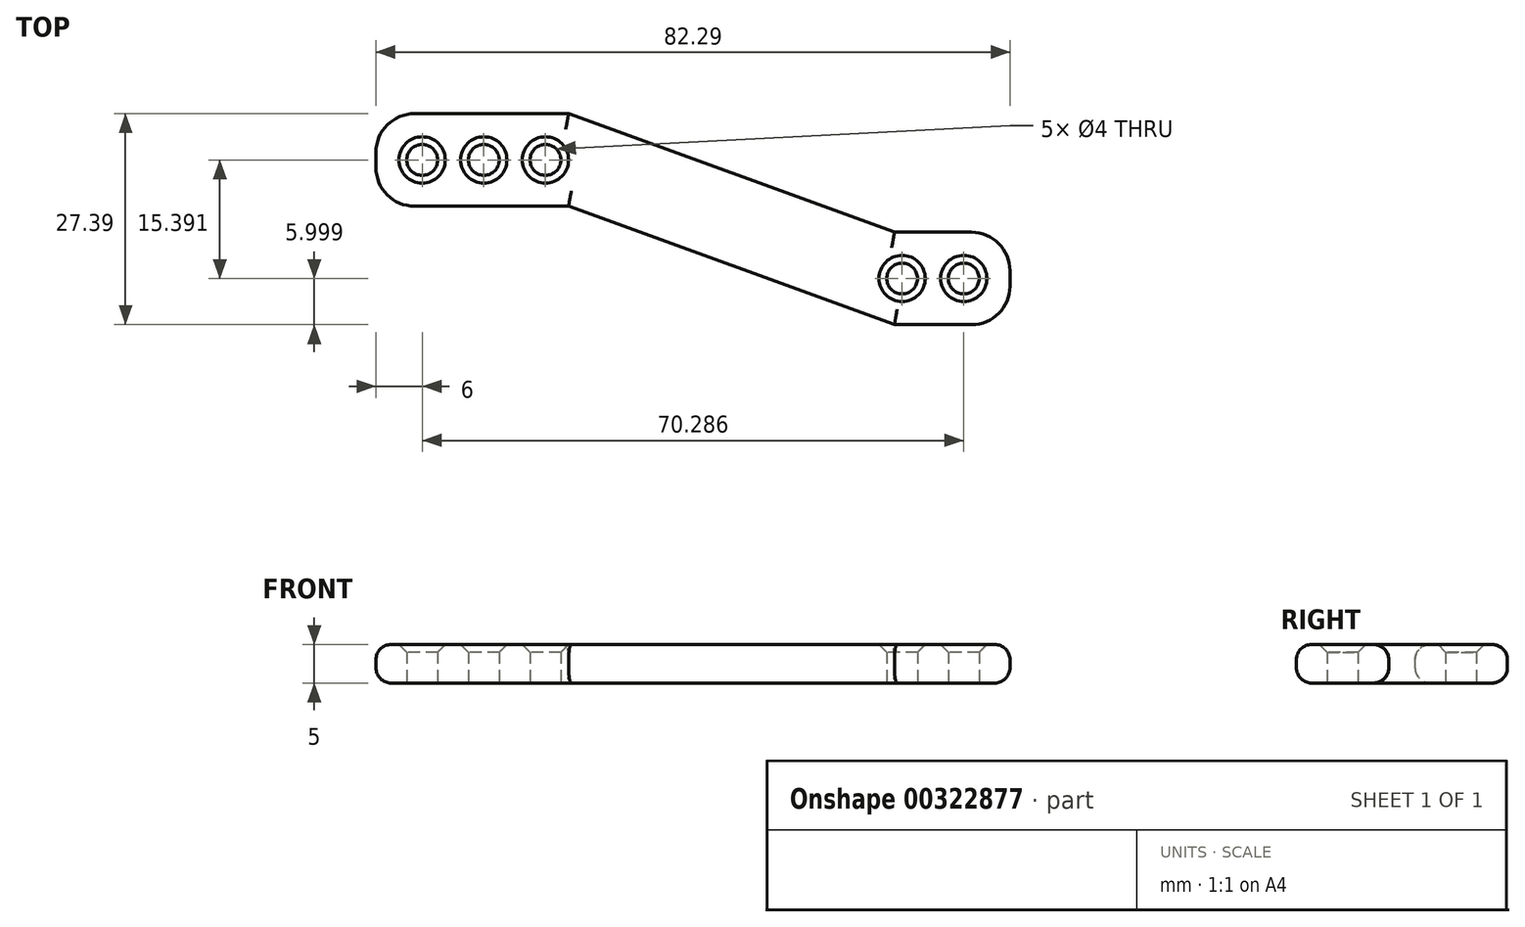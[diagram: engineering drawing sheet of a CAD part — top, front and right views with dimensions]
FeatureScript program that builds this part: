
annotation { "Feature Type Name" : "Feature", "Feature Type Description" : "" }
export const myFeature = defineFeature(function(context is Context, id is Id, definition is map)
    precondition{}
    {
        {
            var Q0;
            Q0=qCreatedBy(makeId("Top.planeOp"),FACE);
            var sketch = newSketch(context, id + "F0", { "sketchPlane" : qUnion([Q0])});
            skLineSegment(sketch, "E0.bottom", {"start": v(0, 0) * mm, "end": v(-25, 0) * mm});
            skLineSegment(sketch, "E0.top", {"start": v(0, -12) * mm, "end": v(-25, -12) * mm});
            skLineSegment(sketch, "E0.left", {"start": v(0, 0) * mm, "end": v(0, -12) * mm});
            skLineSegment(sketch, "E0.right", {"start": v(-25, 0) * mm, "end": v(-25, -12) * mm});
            skLineSegment(sketch, "E1", {"start": v(0, -12) * mm, "end": v(42.29, -27.4) * mm});
            skLineSegment(sketch, "E2", {"start": v(0, 0) * mm, "end": v(42.29, -15.4) * mm});
            skLineSegment(sketch, "E3", {"start": v(42.29, -27.4) * mm, "end": v(42.29, -15.4) * mm});
            skLineSegment(sketch, "E4.bottom", {"start": v(42.29, -27.4) * mm, "end": v(42.29, -27.4) * mm});
            skLineSegment(sketch, "E4.top", {"start": v(42.29, -15.4) * mm, "end": v(42.29, -15.4) * mm});
            skLineSegment(sketch, "E5.bottom", {"start": v(42.29, -27.4) * mm, "end": v(57.29, -27.4) * mm});
            skLineSegment(sketch, "E5.top", {"start": v(42.29, -15.4) * mm, "end": v(57.29, -15.4) * mm});
            skLineSegment(sketch, "E5.right", {"start": v(57.29, -27.4) * mm, "end": v(57.29, -15.4) * mm});
            skSolve(sketch);
        }
        {
            var Q0;
            Q0 = qSketchRegion(id + "F0", true);
            extrude(context, id + "F1", {"entities" : qUnion([Q0]), "depth" : 5 * mm});
        }
        {
            var Q0;
            Q0=qCreatedBy(makeId("Top.planeOp"),FACE);
            var sketch = newSketch(context, id + "F2", { "sketchPlane" : qUnion([Q0])});
            skCircle(sketch, "E6", {"center": v(51.29, -21.4) * mm, "radius": 2 * mm});
            skCircle(sketch, "E7", {"center": v(-19, -6) * mm, "radius": 2 * mm});
            skCircle(sketch, "E8.1.0.0", {"center": v(43.29, -21.4) * mm, "radius": 2 * mm});
            skLineSegment(sketch, "E8.direction1", {"start": v(51.29, -21.4) * mm, "end": v(43.29, -21.4) * mm, "construction": true});
            skCircle(sketch, "E9.1.0.0", {"center": v(-11, -6) * mm, "radius": 2 * mm});
            skCircle(sketch, "E9.2.0.0", {"center": v(-3, -6) * mm, "radius": 2 * mm});
            skLineSegment(sketch, "E9.direction1", {"start": v(-19, -6) * mm, "end": v(-11, -6) * mm, "construction": true});
            skSolve(sketch);
        }
        {
            var Q0;
            Q0 = qSketchRegion(id + "F2", true);
            extrude(context, id + "F3", {"entities" : qUnion([Q0]), "operationType" : NewBodyOperationType.REMOVE, "endBound" : BoundingType.THROUGH_ALL, "depth" : 25 * mm});
        }
        {
            var Q0;
            Q0=makeQuery(id+"F1.opExtrude","CAP_EDGE",EDGE,{"disambiguationData":[OSD([sQuery(id+"F0.wireOp",EDGE,"E1")])],"isStart":false});
            var Q1;
            Q1=makeQuery(id+"F1.opExtrude","CAP_EDGE",EDGE,{"disambiguationData":[OSD([sQuery(id+"F0.wireOp",EDGE,"E2")])],"isStart":false});
            var Q2;
            Q2=makeQuery(id+"F1.opExtrude","CAP_EDGE",EDGE,{"disambiguationData":[OSD([sQuery(id+"F0.wireOp",EDGE,"E0.top")])],"isStart":false});
            var Q3;
            Q3=makeQuery(id+"F1.opExtrude","CAP_EDGE",EDGE,{"disambiguationData":[OSD([sQuery(id+"F0.wireOp",EDGE,"E0.bottom")])],"isStart":false});
            var Q4;
            Q4=makeQuery(id+"F1.opExtrude","CAP_EDGE",EDGE,{"disambiguationData":[OSD([sQuery(id+"F0.wireOp",EDGE,"E5.bottom")])],"isStart":false});
            var Q5;
            Q5=makeQuery(id+"F1.opExtrude","CAP_EDGE",EDGE,{"disambiguationData":[OSD([sQuery(id+"F0.wireOp",EDGE,"E5.right")])],"isStart":false});
            var Q6;
            Q6=makeQuery(id+"F1.opExtrude","CAP_EDGE",EDGE,{"disambiguationData":[OSD([sQuery(id+"F0.wireOp",EDGE,"E5.top")])],"isStart":false});
            var Q7;
            Q7=makeQuery(id+"F1.opExtrude","CAP_EDGE",EDGE,{"disambiguationData":[OSD([sQuery(id+"F0.wireOp",EDGE,"E5.bottom")])],"isStart":true});
            var Q8;
            Q8=makeQuery(id+"F1.opExtrude","CAP_EDGE",EDGE,{"disambiguationData":[OSD([sQuery(id+"F0.wireOp",EDGE,"E1")])],"isStart":true});
            var Q9;
            Q9=makeQuery(id+"F1.opExtrude","CAP_EDGE",EDGE,{"disambiguationData":[OSD([sQuery(id+"F0.wireOp",EDGE,"E0.top")])],"isStart":true});
            var Q10;
            Q10=makeQuery(id+"F1.opExtrude","CAP_EDGE",EDGE,{"disambiguationData":[OSD([sQuery(id+"F0.wireOp",EDGE,"E5.right")])],"isStart":true});
            var Q11;
            Q11=makeQuery(id+"F1.opExtrude","CAP_EDGE",EDGE,{"disambiguationData":[OSD([sQuery(id+"F0.wireOp",EDGE,"E2")])],"isStart":true});
            var Q12;
            Q12=makeQuery(id+"F1.opExtrude","CAP_EDGE",EDGE,{"disambiguationData":[OSD([sQuery(id+"F0.wireOp",EDGE,"E5.top")])],"isStart":true});
            var Q13;
            Q13=makeQuery(id+"F1.opExtrude","CAP_EDGE",EDGE,{"disambiguationData":[OSD([sQuery(id+"F0.wireOp",EDGE,"E0.bottom")])],"isStart":true});
            var Q14;
            Q14=makeQuery(id+"F1.opExtrude","CAP_EDGE",EDGE,{"disambiguationData":[OSD([sQuery(id+"F0.wireOp",EDGE,"E0.right")])],"isStart":true});
            var Q15;
            Q15=makeQuery(id+"F1.opExtrude","CAP_EDGE",EDGE,{"disambiguationData":[OSD([sQuery(id+"F0.wireOp",EDGE,"E0.right")])],"isStart":false});
            fillet(context, id + "F4", {"entities" : qUnion([Q0, Q1, Q2, Q3, Q4, Q5, Q6, Q7, Q8, Q9, Q10, Q11, Q12, Q13, Q14, Q15]), "radius" : 2 * mm, "tangentPropagation" : true, "allowEdgeOverflow" : false});
        }
        {
            var Q0;
            Q0=makeQuery(id+"F1.opExtrude","SWEPT_EDGE",EDGE,{"disambiguationData":[OSD([sQuery(id+"F0.wireOp",EDGE,"E5.top"),sQuery(id+"F0.wireOp",EDGE,"E5.right")])]});
            var Q1;
            Q1=makeQuery(id+"F4.opFillet","BLEND_EDGE",EDGE,{"blendedFrom":[makeQuery(id+"F1.opExtrude","CAP_EDGE",EDGE,{"disambiguationData":[OSD([sQuery(id+"F0.wireOp",EDGE,"E5.bottom")])],"isStart":false}),makeQuery(id+"F1.opExtrude","CAP_EDGE",EDGE,{"disambiguationData":[OSD([sQuery(id+"F0.wireOp",EDGE,"E5.right")])],"isStart":false})],"blendedInto":[]});
            var Q2;
            Q2=makeQuery(id+"F4.opFillet","BLEND_EDGE",EDGE,{"blendedFrom":[makeQuery(id+"F1.opExtrude","CAP_EDGE",EDGE,{"disambiguationData":[OSD([sQuery(id+"F0.wireOp",EDGE,"E0.top")])],"isStart":false}),makeQuery(id+"F1.opExtrude","CAP_EDGE",EDGE,{"disambiguationData":[OSD([sQuery(id+"F0.wireOp",EDGE,"E0.right")])],"isStart":false})],"blendedInto":[]});
            var Q3;
            Q3=makeQuery(id+"F4.opFillet","BLEND_EDGE",EDGE,{"blendedFrom":[makeQuery(id+"F1.opExtrude","CAP_EDGE",EDGE,{"disambiguationData":[OSD([sQuery(id+"F0.wireOp",EDGE,"E0.bottom")])],"isStart":false}),makeQuery(id+"F1.opExtrude","CAP_EDGE",EDGE,{"disambiguationData":[OSD([sQuery(id+"F0.wireOp",EDGE,"E0.right")])],"isStart":false})],"blendedInto":[]});
            fillet(context, id + "F5", {"entities" : qUnion([Q0, Q1, Q2, Q3]), "radius" : 5 * mm, "tangentPropagation" : true, "allowEdgeOverflow" : false});
        }
        {
            var Q0;
            Q0=makeQuery(id+"F3.boolean.opBoolean","INTERSECT",EDGE,{"derivedFrom":[makeQuery(id+"F1.opExtrude","CAP_FACE",FACE,{"disambiguationData":[OSD([sQuery(id+"F0.wireOp",EDGE,"E0.bottom"),sQuery(id+"F0.wireOp",EDGE,"E0.top"),sQuery(id+"F0.wireOp",EDGE,"E0.right"),sQuery(id+"F0.wireOp",EDGE,"E1"),sQuery(id+"F0.wireOp",EDGE,"E2"),sQuery(id+"F0.wireOp",EDGE,"E5.bottom"),sQuery(id+"F0.wireOp",EDGE,"E5.top"),sQuery(id+"F0.wireOp",EDGE,"E5.right")])],"isStart":false}),makeQuery(id+"F3.opExtrude","SWEPT_FACE",FACE,{"disambiguationData":[OSD([sQuery(id+"F2.wireOp",EDGE,"E7")])]})]});
            var Q1;
            Q1=makeQuery(id+"F3.boolean.opBoolean","INTERSECT",EDGE,{"derivedFrom":[makeQuery(id+"F1.opExtrude","CAP_FACE",FACE,{"disambiguationData":[OSD([sQuery(id+"F0.wireOp",EDGE,"E0.bottom"),sQuery(id+"F0.wireOp",EDGE,"E0.top"),sQuery(id+"F0.wireOp",EDGE,"E0.right"),sQuery(id+"F0.wireOp",EDGE,"E1"),sQuery(id+"F0.wireOp",EDGE,"E2"),sQuery(id+"F0.wireOp",EDGE,"E5.bottom"),sQuery(id+"F0.wireOp",EDGE,"E5.top"),sQuery(id+"F0.wireOp",EDGE,"E5.right")])],"isStart":false}),makeQuery(id+"F3.opExtrude","SWEPT_FACE",FACE,{"disambiguationData":[OSD([sQuery(id+"F2.wireOp",EDGE,"E9.1.0.0")])]})]});
            var Q2;
            Q2=makeQuery(id+"F3.boolean.opBoolean","INTERSECT",EDGE,{"derivedFrom":[makeQuery(id+"F1.opExtrude","CAP_FACE",FACE,{"disambiguationData":[OSD([sQuery(id+"F0.wireOp",EDGE,"E0.bottom"),sQuery(id+"F0.wireOp",EDGE,"E0.top"),sQuery(id+"F0.wireOp",EDGE,"E0.right"),sQuery(id+"F0.wireOp",EDGE,"E1"),sQuery(id+"F0.wireOp",EDGE,"E2"),sQuery(id+"F0.wireOp",EDGE,"E5.bottom"),sQuery(id+"F0.wireOp",EDGE,"E5.top"),sQuery(id+"F0.wireOp",EDGE,"E5.right")])],"isStart":false}),makeQuery(id+"F3.opExtrude","SWEPT_FACE",FACE,{"disambiguationData":[OSD([sQuery(id+"F2.wireOp",EDGE,"E9.2.0.0")])]})]});
            var Q3;
            Q3=makeQuery(id+"F3.boolean.opBoolean","INTERSECT",EDGE,{"derivedFrom":[makeQuery(id+"F1.opExtrude","CAP_FACE",FACE,{"disambiguationData":[OSD([sQuery(id+"F0.wireOp",EDGE,"E0.bottom"),sQuery(id+"F0.wireOp",EDGE,"E0.top"),sQuery(id+"F0.wireOp",EDGE,"E0.right"),sQuery(id+"F0.wireOp",EDGE,"E1"),sQuery(id+"F0.wireOp",EDGE,"E2"),sQuery(id+"F0.wireOp",EDGE,"E5.bottom"),sQuery(id+"F0.wireOp",EDGE,"E5.top"),sQuery(id+"F0.wireOp",EDGE,"E5.right")])],"isStart":false}),makeQuery(id+"F3.opExtrude","SWEPT_FACE",FACE,{"disambiguationData":[OSD([sQuery(id+"F2.wireOp",EDGE,"E8.1.0.0")])]})]});
            var Q4;
            Q4=makeQuery(id+"F3.boolean.opBoolean","INTERSECT",EDGE,{"derivedFrom":[makeQuery(id+"F1.opExtrude","CAP_FACE",FACE,{"disambiguationData":[OSD([sQuery(id+"F0.wireOp",EDGE,"E0.bottom"),sQuery(id+"F0.wireOp",EDGE,"E0.top"),sQuery(id+"F0.wireOp",EDGE,"E0.right"),sQuery(id+"F0.wireOp",EDGE,"E1"),sQuery(id+"F0.wireOp",EDGE,"E2"),sQuery(id+"F0.wireOp",EDGE,"E5.bottom"),sQuery(id+"F0.wireOp",EDGE,"E5.top"),sQuery(id+"F0.wireOp",EDGE,"E5.right")])],"isStart":false}),makeQuery(id+"F3.opExtrude","SWEPT_FACE",FACE,{"disambiguationData":[OSD([sQuery(id+"F2.wireOp",EDGE,"E6")])]})]});
            chamfer(context, id + "F6", {"entities" : qUnion([Q0, Q1, Q2, Q3, Q4]), "width" : 1 * mm, "tangentPropagation" : true});
        }
    });
